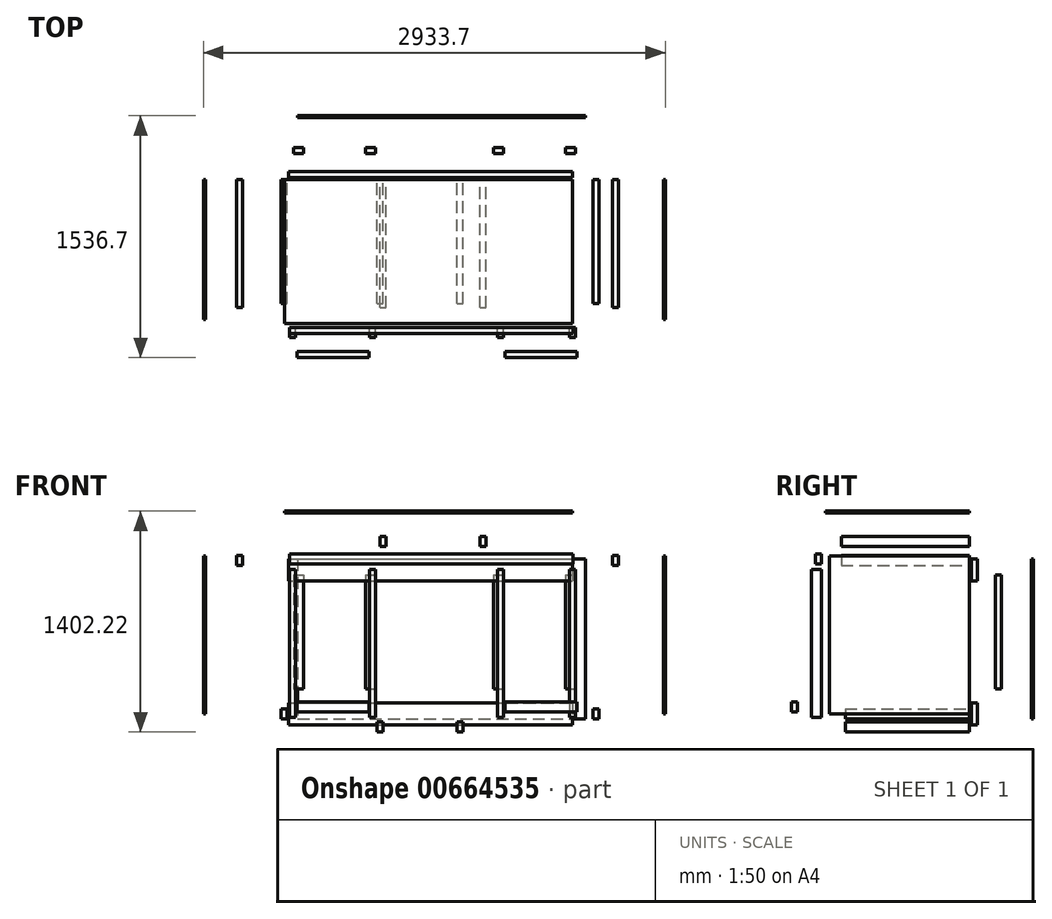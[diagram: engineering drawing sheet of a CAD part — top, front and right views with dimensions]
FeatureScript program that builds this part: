
annotation { "Feature Type Name" : "Feature", "Feature Type Description" : "" }
export const myFeature = defineFeature(function(context is Context, id is Id, definition is map)
    precondition{}
    {
        {
            var Q0;
            Q0=qCreatedBy(makeId("Front.planeOp"),FACE);
            var sketch = newSketch(context, id + "F0", { "sketchPlane" : qUnion([Q0])});
            skLineSegment(sketch, "E0.bottom", {"start": v(-77.6, 167.5) * mm, "end": v(1751.2, 167.5) * mm});
            skLineSegment(sketch, "E0.top", {"start": v(-77.6, 154.8) * mm, "end": v(1751.2, 154.8) * mm});
            skLineSegment(sketch, "E0.left", {"start": v(-77.6, 167.5) * mm, "end": v(-77.6, 154.8) * mm});
            skLineSegment(sketch, "E0.right", {"start": v(1751.2, 167.5) * mm, "end": v(1751.2, 154.8) * mm});
            skSolve(sketch);
        }
        {
            var Q0;
            Q0 = qSketchRegion(id + "F0", true);
            extrude(context, id + "F1", {"entities" : qUnion([Q0]), "depth" : 914.4 * mm, "offsetDistance" : 25.4 * mm});
        }
        {
            var Q0;
            Q0=qCreatedBy(makeId("Front.planeOp"),FACE);
            var sketch = newSketch(context, id + "F2", { "sketchPlane" : qUnion([Q0])});
            skLineSegment(sketch, "E1.bottom", {"start": v(-96.67, 148.12) * mm, "end": v(1706.73, 148.12) * mm});
            skLineSegment(sketch, "E1.top", {"start": v(-96.67, 84.62) * mm, "end": v(1706.73, 84.62) * mm});
            skLineSegment(sketch, "E1.left", {"start": v(-96.67, 148.12) * mm, "end": v(-96.67, 84.62) * mm});
            skLineSegment(sketch, "E1.right", {"start": v(1706.73, 148.12) * mm, "end": v(1706.73, 84.62) * mm});
            skSolve(sketch);
        }
        {
            var Q0;
            Q0 = qSketchRegion(id + "F2", true);
            extrude(context, id + "F3", {"entities" : qUnion([Q0]), "depth" : 38.1 * mm, "offsetDistance" : 25.4 * mm});
        }
        {
            var Q0;
            Q0=makeQuery(id+"F3.opExtrude","SWEPT_BODY",BODY,{"disambiguationData":[OSD([sQuery(id+"F2.wireOp",EDGE,"E1.bottom"),sQuery(id+"F2.wireOp",EDGE,"E1.top"),sQuery(id+"F2.wireOp",EDGE,"E1.left"),sQuery(id+"F2.wireOp",EDGE,"E1.right")])]});
            transform(context, id + "F4", {"entities" : qUnion([Q0]), "transformType" : TransformType.TRANSLATION_3D, "dx" : -762 * mm, "dy" : -939.8 * mm, "dz" : 0 * mm, "makeCopy" : false});
        }
        {
            var Q0;
            Q0=makeQuery(id+"F1.opExtrude","SWEPT_BODY",BODY,{"disambiguationData":[OSD([sQuery(id+"F0.wireOp",EDGE,"E0.bottom"),sQuery(id+"F0.wireOp",EDGE,"E0.top"),sQuery(id+"F0.wireOp",EDGE,"E0.left"),sQuery(id+"F0.wireOp",EDGE,"E0.right")])]});
            transform(context, id + "F5", {"entities" : qUnion([Q0]), "transformType" : TransformType.TRANSLATION_3D, "dx" : -812.8 * mm, "dy" : 0 * mm, "dz" : 0 * mm, "makeCopy" : false});
        }
        {
            var Q0;
            Q0=qCreatedBy(makeId("Front.planeOp"),FACE);
            var sketch = newSketch(context, id + "F6", { "sketchPlane" : qUnion([Q0])});
            skLineSegment(sketch, "E2.bottom", {"start": v(-857.8, 557.43) * mm, "end": v(-819.7, 557.43) * mm});
            skLineSegment(sketch, "E2.top", {"start": v(-857.8, -382.37) * mm, "end": v(-819.7, -382.37) * mm});
            skLineSegment(sketch, "E2.left", {"start": v(-857.8, 557.43) * mm, "end": v(-857.8, -382.37) * mm});
            skLineSegment(sketch, "E2.right", {"start": v(-819.7, 557.43) * mm, "end": v(-819.7, -382.37) * mm});
            skSolve(sketch);
        }
        {
            var Q0;
            Q0 = qSketchRegion(id + "F6", true);
            extrude(context, id + "F7", {"entities" : qUnion([Q0]), "depth" : 63.5 * mm, "offsetDistance" : 25.4 * mm});
        }
        {
            var Q0;
            Q0=makeQuery(id+"F7.opExtrude","SWEPT_BODY",BODY,{"disambiguationData":[OSD([sQuery(id+"F6.wireOp",EDGE,"E2.bottom"),sQuery(id+"F6.wireOp",EDGE,"E2.top"),sQuery(id+"F6.wireOp",EDGE,"E2.left"),sQuery(id+"F6.wireOp",EDGE,"E2.right")])]});
            transform(context, id + "F8", {"entities" : qUnion([Q0]), "transformType" : TransformType.TRANSLATION_3D, "dx" : 0 * mm, "dy" : -939.8 * mm, "dz" : -508 * mm, "makeCopy" : false});
        }
        {
            var Q0;
            Q0=makeQuery(id+"F7.opExtrude","SWEPT_BODY",BODY,{"disambiguationData":[OSD([sQuery(id+"F6.wireOp",EDGE,"E2.bottom"),sQuery(id+"F6.wireOp",EDGE,"E2.top"),sQuery(id+"F6.wireOp",EDGE,"E2.left"),sQuery(id+"F6.wireOp",EDGE,"E2.right")])]});
            transform(context, id + "F9", {"entities" : qUnion([Q0]), "transformType" : TransformType.TRANSLATION_3D, "dx" : 1778 * mm, "dy" : 0 * mm, "dz" : 0 * mm, "makeCopy" : true});
        }
        {
            var Q0;
            Q0=makeQuery(id+"F7.opExtrude","SWEPT_BODY",BODY,{"disambiguationData":[OSD([sQuery(id+"F6.wireOp",EDGE,"E2.bottom"),sQuery(id+"F6.wireOp",EDGE,"E2.top"),sQuery(id+"F6.wireOp",EDGE,"E2.left"),sQuery(id+"F6.wireOp",EDGE,"E2.right")])]});
            transform(context, id + "F10", {"entities" : qUnion([Q0]), "transformType" : TransformType.TRANSLATION_3D, "dx" : 508 * mm, "dy" : 0 * mm, "dz" : 0 * mm, "makeCopy" : true});
        }
        {
            var Q0;
            Q0=makeQuery(id+"F7.opExtrude","SWEPT_BODY",BODY,{"disambiguationData":[OSD([sQuery(id+"F6.wireOp",EDGE,"E2.bottom"),sQuery(id+"F6.wireOp",EDGE,"E2.top"),sQuery(id+"F6.wireOp",EDGE,"E2.left"),sQuery(id+"F6.wireOp",EDGE,"E2.right")])]});
            transform(context, id + "F11", {"entities" : qUnion([Q0]), "transformType" : TransformType.TRANSLATION_3D, "dx" : 1320.8 * mm, "dy" : 0 * mm, "dz" : 0 * mm, "makeCopy" : true});
        }
        {
            var Q0;
            Q0=qCreatedBy(makeId("Front.planeOp"),FACE);
            var sketch = newSketch(context, id + "F12", { "sketchPlane" : qUnion([Q0])});
            skLineSegment(sketch, "E3.bottom", {"start": v(-940.02, 138.97) * mm, "end": v(-901.92, 138.97) * mm});
            skLineSegment(sketch, "E3.top", {"start": v(-940.02, 75.47) * mm, "end": v(-901.92, 75.47) * mm});
            skLineSegment(sketch, "E3.left", {"start": v(-940.02, 138.97) * mm, "end": v(-940.02, 75.47) * mm});
            skLineSegment(sketch, "E3.right", {"start": v(-901.92, 138.97) * mm, "end": v(-901.92, 75.47) * mm});
            skSolve(sketch);
        }
        {
            var Q0;
            Q0 = qSketchRegion(id + "F12", true);
            extrude(context, id + "F13", {"entities" : qUnion([Q0]), "depth" : 812.8 * mm, "offsetDistance" : 25.4 * mm});
        }
        {
            var Q0;
            Q0=makeQuery(id+"F13.opExtrude","SWEPT_BODY",BODY,{"disambiguationData":[OSD([sQuery(id+"F12.wireOp",EDGE,"E3.bottom"),sQuery(id+"F12.wireOp",EDGE,"E3.top"),sQuery(id+"F12.wireOp",EDGE,"E3.left"),sQuery(id+"F12.wireOp",EDGE,"E3.right")])]});
            transform(context, id + "F14", {"entities" : qUnion([Q0]), "transformType" : TransformType.TRANSLATION_3D, "dx" : 1879.6 * mm, "dy" : 0 * mm, "dz" : 0 * mm, "makeCopy" : true});
        }
        {
            var Q0;
            Q0=qCreatedBy(makeId("Front.planeOp"),FACE);
            var sketch = newSketch(context, id + "F15", { "sketchPlane" : qUnion([Q0])});
            skLineSegment(sketch, "E4.bottom", {"start": v(-862.45, 42) * mm, "end": v(940.95, 42) * mm});
            skLineSegment(sketch, "E4.top", {"start": v(-862.45, -97.7) * mm, "end": v(940.95, -97.7) * mm});
            skLineSegment(sketch, "E4.left", {"start": v(-862.45, 42) * mm, "end": v(-862.45, -97.7) * mm});
            skLineSegment(sketch, "E4.right", {"start": v(940.95, 42) * mm, "end": v(940.95, -97.7) * mm});
            skSolve(sketch);
        }
        {
            var Q0;
            Q0 = qSketchRegion(id + "F15", true);
            extrude(context, id + "F16", {"entities" : qUnion([Q0]), "depth" : 38.1 * mm, "offsetDistance" : 25.4 * mm});
        }
        {
            var Q0;
            Q0=makeQuery(id+"F16.opExtrude","SWEPT_BODY",BODY,{"disambiguationData":[OSD([sQuery(id+"F15.wireOp",EDGE,"E4.bottom"),sQuery(id+"F15.wireOp",EDGE,"E4.top"),sQuery(id+"F15.wireOp",EDGE,"E4.left"),sQuery(id+"F15.wireOp",EDGE,"E4.right")])]});
            transform(context, id + "F17", {"entities" : qUnion([Q0]), "transformType" : TransformType.TRANSLATION_3D, "dx" : 0 * mm, "dy" : 0 * mm, "dz" : -762 * mm, "makeCopy" : true});
        }
        {
            var Q0;
            Q0=makeQuery(id+"F13.opExtrude","SWEPT_BODY",BODY,{"disambiguationData":[OSD([sQuery(id+"F12.wireOp",EDGE,"E3.bottom"),sQuery(id+"F12.wireOp",EDGE,"E3.top"),sQuery(id+"F12.wireOp",EDGE,"E3.left"),sQuery(id+"F12.wireOp",EDGE,"E3.right")])]});
            transform(context, id + "F18", {"entities" : qUnion([Q0]), "transformType" : TransformType.TRANSLATION_3D, "dx" : 0 * mm, "dy" : 0 * mm, "dz" : -939.8 * mm, "makeCopy" : true});
        }
        {
            var Q0;
            Q0=makeQuery(id+"F14.opPattern","COPY",BODY,{"derivedFrom":makeQuery(id+"F13.opExtrude","SWEPT_BODY",BODY,{"disambiguationData":[OSD([sQuery(id+"F12.wireOp",EDGE,"E3.bottom"),sQuery(id+"F12.wireOp",EDGE,"E3.top"),sQuery(id+"F12.wireOp",EDGE,"E3.left"),sQuery(id+"F12.wireOp",EDGE,"E3.right")])]}),"instanceName":"1"});
            transform(context, id + "F19", {"entities" : qUnion([Q0]), "transformType" : TransformType.TRANSLATION_3D, "dx" : 0 * mm, "dy" : 0 * mm, "dz" : -939.8 * mm, "makeCopy" : true});
        }
        {
            var Q0;
            Q0=qCreatedBy(makeId("Front.planeOp"),FACE);
            var sketch = newSketch(context, id + "F20", { "sketchPlane" : qUnion([Q0])});
            skLineSegment(sketch, "E5.bottom", {"start": v(-809.8, -791.75) * mm, "end": v(-352.6, -791.75) * mm});
            skLineSegment(sketch, "E5.top", {"start": v(-809.8, -855.25) * mm, "end": v(-352.6, -855.25) * mm});
            skLineSegment(sketch, "E5.left", {"start": v(-809.8, -791.75) * mm, "end": v(-809.8, -855.25) * mm});
            skLineSegment(sketch, "E5.right", {"start": v(-352.6, -791.75) * mm, "end": v(-352.6, -855.25) * mm});
            skSolve(sketch);
        }
        {
            var Q0;
            Q0 = qSketchRegion(id + "F20", true);
            extrude(context, id + "F21", {"entities" : qUnion([Q0]), "depth" : 38.1 * mm, "offsetDistance" : 25.4 * mm});
        }
        {
            var Q0;
            Q0=makeQuery(id+"F21.opExtrude","SWEPT_BODY",BODY,{"disambiguationData":[OSD([sQuery(id+"F20.wireOp",EDGE,"E5.bottom"),sQuery(id+"F20.wireOp",EDGE,"E5.top"),sQuery(id+"F20.wireOp",EDGE,"E5.left"),sQuery(id+"F20.wireOp",EDGE,"E5.right")])]});
            transform(context, id + "F22", {"entities" : qUnion([Q0]), "transformType" : TransformType.TRANSLATION_3D, "dx" : 0 * mm, "dy" : -965.2 * mm, "dz" : 0 * mm, "makeCopy" : false});
        }
        {
            var Q0;
            Q0=makeQuery(id+"F21.opExtrude","SWEPT_BODY",BODY,{"disambiguationData":[OSD([sQuery(id+"F20.wireOp",EDGE,"E5.bottom"),sQuery(id+"F20.wireOp",EDGE,"E5.top"),sQuery(id+"F20.wireOp",EDGE,"E5.left"),sQuery(id+"F20.wireOp",EDGE,"E5.right")])]});
            transform(context, id + "F23", {"entities" : qUnion([Q0]), "transformType" : TransformType.TRANSLATION_3D, "dx" : 1320.8 * mm, "dy" : 0 * mm, "dz" : 0 * mm, "makeCopy" : true});
        }
        {
            var Q0;
            Q0=makeQuery(id+"F13.opExtrude","SWEPT_BODY",BODY,{"disambiguationData":[OSD([sQuery(id+"F12.wireOp",EDGE,"E3.bottom"),sQuery(id+"F12.wireOp",EDGE,"E3.top"),sQuery(id+"F12.wireOp",EDGE,"E3.left"),sQuery(id+"F12.wireOp",EDGE,"E3.right")])]});
            transform(context, id + "F24", {"entities" : qUnion([Q0]), "transformType" : TransformType.TRANSLATION_3D, "dx" : 508 * mm, "dy" : 0 * mm, "dz" : 0 * mm, "makeCopy" : true});
        }
        {
            var Q0;
            Q0=makeQuery(id+"F13.opExtrude","SWEPT_BODY",BODY,{"disambiguationData":[OSD([sQuery(id+"F12.wireOp",EDGE,"E3.bottom"),sQuery(id+"F12.wireOp",EDGE,"E3.top"),sQuery(id+"F12.wireOp",EDGE,"E3.left"),sQuery(id+"F12.wireOp",EDGE,"E3.right")])]});
            transform(context, id + "F25", {"entities" : qUnion([Q0]), "transformType" : TransformType.TRANSLATION_3D, "dx" : 1320.8 * mm, "dy" : 0 * mm, "dz" : 0 * mm, "makeCopy" : true});
        }
        {
            var Q0;
            Q0=qCreatedBy(makeId("Front.planeOp"),FACE);
            var sketch = newSketch(context, id + "F26", { "sketchPlane" : qUnion([Q0])});
            skLineSegment(sketch, "E6.bottom", {"start": v(-831.16, 15.51) * mm, "end": v(-767.66, 15.51) * mm});
            skLineSegment(sketch, "E6.top", {"start": v(-831.16, -708.39) * mm, "end": v(-767.66, -708.39) * mm});
            skLineSegment(sketch, "E6.left", {"start": v(-831.16, 15.51) * mm, "end": v(-831.16, -708.39) * mm});
            skLineSegment(sketch, "E6.right", {"start": v(-767.66, 15.51) * mm, "end": v(-767.66, -708.39) * mm});
            skSolve(sketch);
        }
        {
            var Q0;
            Q0 = qSketchRegion(id + "F26", true);
            extrude(context, id + "F27", {"entities" : qUnion([Q0]), "depth" : 38.1 * mm, "offsetDistance" : 25.4 * mm});
        }
        {
            var Q0;
            Q0=makeQuery(id+"F27.opExtrude","SWEPT_BODY",BODY,{"disambiguationData":[OSD([sQuery(id+"F26.wireOp",EDGE,"E6.bottom"),sQuery(id+"F26.wireOp",EDGE,"E6.top"),sQuery(id+"F26.wireOp",EDGE,"E6.left"),sQuery(id+"F26.wireOp",EDGE,"E6.right")])]});
            transform(context, id + "F28", {"entities" : qUnion([Q0]), "transformType" : TransformType.TRANSLATION_3D, "dx" : 0 * mm, "dy" : 76.2 * mm, "dz" : 0 * mm, "makeCopy" : false});
        }
        {
            var Q0;
            Q0=makeQuery(id+"F27.opExtrude","SWEPT_BODY",BODY,{"disambiguationData":[OSD([sQuery(id+"F26.wireOp",EDGE,"E6.bottom"),sQuery(id+"F26.wireOp",EDGE,"E6.top"),sQuery(id+"F26.wireOp",EDGE,"E6.left"),sQuery(id+"F26.wireOp",EDGE,"E6.right")])]});
            transform(context, id + "F29", {"entities" : qUnion([Q0]), "transformType" : TransformType.TRANSLATION_3D, "dx" : 457.2 * mm, "dy" : 0 * mm, "dz" : 0 * mm, "makeCopy" : true});
        }
        {
            var Q0;
            Q0=makeQuery(id+"F27.opExtrude","SWEPT_BODY",BODY,{"disambiguationData":[OSD([sQuery(id+"F26.wireOp",EDGE,"E6.bottom"),sQuery(id+"F26.wireOp",EDGE,"E6.top"),sQuery(id+"F26.wireOp",EDGE,"E6.left"),sQuery(id+"F26.wireOp",EDGE,"E6.right")])]});
            transform(context, id + "F30", {"entities" : qUnion([Q0]), "transformType" : TransformType.TRANSLATION_3D, "dx" : 1270 * mm, "dy" : 0 * mm, "dz" : 0 * mm, "makeCopy" : true});
        }
        {
            var Q0;
            Q0=makeQuery(id+"F27.opExtrude","SWEPT_BODY",BODY,{"disambiguationData":[OSD([sQuery(id+"F26.wireOp",EDGE,"E6.bottom"),sQuery(id+"F26.wireOp",EDGE,"E6.top"),sQuery(id+"F26.wireOp",EDGE,"E6.left"),sQuery(id+"F26.wireOp",EDGE,"E6.right")])]});
            transform(context, id + "F31", {"entities" : qUnion([Q0]), "transformType" : TransformType.TRANSLATION_3D, "dx" : 1727.2 * mm, "dy" : 0 * mm, "dz" : 0 * mm, "makeCopy" : true});
        }
        {
            var Q0;
            Q0=qCreatedBy(makeId("Front.planeOp"),FACE);
            var sketch = newSketch(context, id + "F32", { "sketchPlane" : qUnion([Q0])});
            skLineSegment(sketch, "E7.bottom", {"start": v(-1023.09, 135.28) * mm, "end": v(-1010.39, 135.28) * mm});
            skLineSegment(sketch, "E7.top", {"start": v(-1023.09, -868.02) * mm, "end": v(-1010.39, -868.02) * mm});
            skLineSegment(sketch, "E7.left", {"start": v(-1023.09, 135.28) * mm, "end": v(-1023.09, -868.02) * mm});
            skLineSegment(sketch, "E7.right", {"start": v(-1010.39, 135.28) * mm, "end": v(-1010.39, -868.02) * mm});
            skSolve(sketch);
        }
        {
            var Q0;
            Q0 = qSketchRegion(id + "F32", true);
            extrude(context, id + "F33", {"entities" : qUnion([Q0]), "depth" : 889 * mm, "offsetDistance" : 25.4 * mm});
        }
        {
            var Q0;
            Q0=makeQuery(id+"F33.opExtrude","SWEPT_BODY",BODY,{"disambiguationData":[OSD([sQuery(id+"F32.wireOp",EDGE,"E7.bottom"),sQuery(id+"F32.wireOp",EDGE,"E7.top"),sQuery(id+"F32.wireOp",EDGE,"E7.left"),sQuery(id+"F32.wireOp",EDGE,"E7.right")])]});
            transform(context, id + "F34", {"entities" : qUnion([Q0]), "transformType" : TransformType.TRANSLATION_3D, "dx" : 2032 * mm, "dy" : 0 * mm, "dz" : 0 * mm, "makeCopy" : true});
        }
        {
            var Q0;
            Q0=qCreatedBy(makeId("Front.planeOp"),FACE);
            var sketch = newSketch(context, id + "F35", { "sketchPlane" : qUnion([Q0])});
            skLineSegment(sketch, "E8.bottom", {"start": v(-806.57, 117.24) * mm, "end": v(1022.23, 117.24) * mm});
            skLineSegment(sketch, "E8.top", {"start": v(-806.57, -898.76) * mm, "end": v(1022.23, -898.76) * mm});
            skLineSegment(sketch, "E8.left", {"start": v(-806.57, 117.24) * mm, "end": v(-806.57, -898.76) * mm});
            skLineSegment(sketch, "E8.right", {"start": v(1022.23, 117.24) * mm, "end": v(1022.23, -898.76) * mm});
            skSolve(sketch);
        }
        {
            var Q0;
            Q0 = qSketchRegion(id + "F35", true);
            extrude(context, id + "F36", {"entities" : qUnion([Q0]), "depth" : 12.7 * mm, "offsetDistance" : 25.4 * mm});
        }
        {
            var Q0;
            Q0=makeQuery(id+"F36.opExtrude","SWEPT_BODY",BODY,{"disambiguationData":[OSD([sQuery(id+"F35.wireOp",EDGE,"E8.bottom"),sQuery(id+"F35.wireOp",EDGE,"E8.top"),sQuery(id+"F35.wireOp",EDGE,"E8.left"),sQuery(id+"F35.wireOp",EDGE,"E8.right")])]});
            transform(context, id + "F37", {"entities" : qUnion([Q0]), "transformType" : TransformType.TRANSLATION_3D, "dx" : 0 * mm, "dy" : 152.4 * mm, "dz" : 0 * mm, "makeCopy" : false});
        }
        {
            var Q0;
            Q0=qCreatedBy(makeId("Front.planeOp"),FACE);
            var sketch = newSketch(context, id + "F38", { "sketchPlane" : qUnion([Q0])});
            skLineSegment(sketch, "E9.bottom", {"start": v(-300.73, -790.22) * mm, "end": v(-262.63, -790.22) * mm});
            skLineSegment(sketch, "E9.top", {"start": v(-300.73, -853.72) * mm, "end": v(-262.63, -853.72) * mm});
            skLineSegment(sketch, "E9.left", {"start": v(-300.73, -790.22) * mm, "end": v(-300.73, -853.72) * mm});
            skLineSegment(sketch, "E9.right", {"start": v(-262.63, -790.22) * mm, "end": v(-262.63, -853.72) * mm});
            skSolve(sketch);
        }
        {
            var Q0;
            Q0 = qSketchRegion(id + "F38", true);
            extrude(context, id + "F39", {"entities" : qUnion([Q0]), "depth" : 787.4 * mm, "offsetDistance" : 25.4 * mm});
        }
        {
            var Q0;
            Q0=makeQuery(id+"F39.opExtrude","SWEPT_BODY",BODY,{"disambiguationData":[OSD([sQuery(id+"F38.wireOp",EDGE,"E9.bottom"),sQuery(id+"F38.wireOp",EDGE,"E9.top"),sQuery(id+"F38.wireOp",EDGE,"E9.left"),sQuery(id+"F38.wireOp",EDGE,"E9.right")])]});
            transform(context, id + "F40", {"entities" : qUnion([Q0]), "transformType" : TransformType.TRANSLATION_3D, "dx" : 508 * mm, "dy" : 0 * mm, "dz" : 0 * mm, "makeCopy" : true});
        }
        {
            var Q0;
            Q0=makeQuery(id+"F19.opPattern","COPY",BODY,{"derivedFrom":makeQuery(id+"F14.opPattern","COPY",BODY,{"derivedFrom":makeQuery(id+"F13.opExtrude","SWEPT_BODY",BODY,{"disambiguationData":[OSD([sQuery(id+"F12.wireOp",EDGE,"E3.bottom"),sQuery(id+"F12.wireOp",EDGE,"E3.top"),sQuery(id+"F12.wireOp",EDGE,"E3.left"),sQuery(id+"F12.wireOp",EDGE,"E3.right")])]}),"instanceName":"1"}),"instanceName":"1"});
            deleteBodies(context, id + "F41", {"entities" : qUnion([Q0])});
        }
        {
            var Q0;
            Q0=makeQuery(id+"F18.opPattern","COPY",BODY,{"derivedFrom":makeQuery(id+"F13.opExtrude","SWEPT_BODY",BODY,{"disambiguationData":[OSD([sQuery(id+"F12.wireOp",EDGE,"E3.bottom"),sQuery(id+"F12.wireOp",EDGE,"E3.top"),sQuery(id+"F12.wireOp",EDGE,"E3.left"),sQuery(id+"F12.wireOp",EDGE,"E3.right")])]}),"instanceName":"1"});
            deleteBodies(context, id + "F42", {"entities" : qUnion([Q0])});
        }
        {
            var Q0;
            Q0=makeQuery(id+"F24.opPattern","COPY",BODY,{"derivedFrom":makeQuery(id+"F13.opExtrude","SWEPT_BODY",BODY,{"disambiguationData":[OSD([sQuery(id+"F12.wireOp",EDGE,"E3.bottom"),sQuery(id+"F12.wireOp",EDGE,"E3.top"),sQuery(id+"F12.wireOp",EDGE,"E3.left"),sQuery(id+"F12.wireOp",EDGE,"E3.right")])]}),"instanceName":"1"});
            deleteBodies(context, id + "F43", {"entities" : qUnion([Q0])});
        }
        {
            var Q0;
            Q0=makeQuery(id+"F25.opPattern","COPY",BODY,{"derivedFrom":makeQuery(id+"F13.opExtrude","SWEPT_BODY",BODY,{"disambiguationData":[OSD([sQuery(id+"F12.wireOp",EDGE,"E3.bottom"),sQuery(id+"F12.wireOp",EDGE,"E3.top"),sQuery(id+"F12.wireOp",EDGE,"E3.left"),sQuery(id+"F12.wireOp",EDGE,"E3.right")])]}),"instanceName":"1"});
            deleteBodies(context, id + "F44", {"entities" : qUnion([Q0])});
        }
        {
            var Q0;
            Q0=qCreatedBy(makeId("Front.planeOp"),FACE);
            var sketch = newSketch(context, id + "F45", { "sketchPlane" : qUnion([Q0])});
            skLineSegment(sketch, "E10.bottom", {"start": v(-911.41, -835.62) * mm, "end": v(-873.31, -835.62) * mm});
            skLineSegment(sketch, "E10.top", {"start": v(-911.41, -899.12) * mm, "end": v(-873.31, -899.12) * mm});
            skLineSegment(sketch, "E10.left", {"start": v(-911.41, -835.62) * mm, "end": v(-911.41, -899.12) * mm});
            skLineSegment(sketch, "E10.right", {"start": v(-873.31, -835.62) * mm, "end": v(-873.31, -899.12) * mm});
            skSolve(sketch);
        }
        {
            var Q0;
            Q0 = qSketchRegion(id + "F45", true);
            extrude(context, id + "F46", {"entities" : qUnion([Q0]), "depth" : 787.4 * mm, "offsetDistance" : 25.4 * mm});
        }
        {
            var Q0;
            Q0=makeQuery(id+"F46.opExtrude","SWEPT_BODY",BODY,{"disambiguationData":[OSD([sQuery(id+"F45.wireOp",EDGE,"E10.bottom"),sQuery(id+"F45.wireOp",EDGE,"E10.top"),sQuery(id+"F45.wireOp",EDGE,"E10.left"),sQuery(id+"F45.wireOp",EDGE,"E10.right")])]});
            transform(context, id + "F47", {"entities" : qUnion([Q0]), "transformType" : TransformType.TRANSLATION_3D, "dx" : 1981.2 * mm, "dy" : 0 * mm, "dz" : 0 * mm, "makeCopy" : true});
        }
        {
            var Q0;
            Q0=makeQuery(id+"F46.opExtrude","SWEPT_BODY",BODY,{"disambiguationData":[OSD([sQuery(id+"F45.wireOp",EDGE,"E10.bottom"),sQuery(id+"F45.wireOp",EDGE,"E10.top"),sQuery(id+"F45.wireOp",EDGE,"E10.left"),sQuery(id+"F45.wireOp",EDGE,"E10.right")])]});
            transform(context, id + "F48", {"entities" : qUnion([Q0]), "transformType" : TransformType.TRANSLATION_3D, "dx" : 533.4 * mm, "dy" : 0 * mm, "dz" : 762 * mm, "makeCopy" : true});
        }
        {
            var Q0;
            Q0=makeQuery(id+"F48.opPattern","COPY",BODY,{"derivedFrom":makeQuery(id+"F46.opExtrude","SWEPT_BODY",BODY,{"disambiguationData":[OSD([sQuery(id+"F45.wireOp",EDGE,"E10.bottom"),sQuery(id+"F45.wireOp",EDGE,"E10.top"),sQuery(id+"F45.wireOp",EDGE,"E10.left"),sQuery(id+"F45.wireOp",EDGE,"E10.right")])]}),"instanceName":"1"});
            transform(context, id + "F49", {"entities" : qUnion([Q0]), "transformType" : TransformType.TRANSLATION_3D, "dx" : 635 * mm, "dy" : 0 * mm, "dz" : 0 * mm, "makeCopy" : true});
        }
        {
            var Q0;
            Q0=makeQuery(id+"F48.opPattern","COPY",BODY,{"derivedFrom":makeQuery(id+"F46.opExtrude","SWEPT_BODY",BODY,{"disambiguationData":[OSD([sQuery(id+"F45.wireOp",EDGE,"E10.bottom"),sQuery(id+"F45.wireOp",EDGE,"E10.top"),sQuery(id+"F45.wireOp",EDGE,"E10.left"),sQuery(id+"F45.wireOp",EDGE,"E10.right")])]}),"instanceName":"1"});
            deleteBodies(context, id + "F50", {"entities" : qUnion([Q0])});
        }
        {
            var Q0;
            Q0=makeQuery(id+"F49.opPattern","COPY",BODY,{"derivedFrom":makeQuery(id+"F48.opPattern","COPY",BODY,{"derivedFrom":makeQuery(id+"F46.opExtrude","SWEPT_BODY",BODY,{"disambiguationData":[OSD([sQuery(id+"F45.wireOp",EDGE,"E10.bottom"),sQuery(id+"F45.wireOp",EDGE,"E10.top"),sQuery(id+"F45.wireOp",EDGE,"E10.left"),sQuery(id+"F45.wireOp",EDGE,"E10.right")])]}),"instanceName":"1"}),"instanceName":"1"});
            deleteBodies(context, id + "F51", {"entities" : qUnion([Q0])});
        }
        {
            var Q0;
            Q0=qCreatedBy(makeId("Front.planeOp"),FACE);
            var sketch = newSketch(context, id + "F52", { "sketchPlane" : qUnion([Q0])});
            skLineSegment(sketch, "E11.bottom", {"start": v(-283.08, 7.53) * mm, "end": v(-244.98, 7.53) * mm});
            skLineSegment(sketch, "E11.top", {"start": v(-283.08, -55.97) * mm, "end": v(-244.98, -55.97) * mm});
            skLineSegment(sketch, "E11.left", {"start": v(-283.08, 7.53) * mm, "end": v(-283.08, -55.97) * mm});
            skLineSegment(sketch, "E11.right", {"start": v(-244.98, 7.53) * mm, "end": v(-244.98, -55.97) * mm});
            skSolve(sketch);
        }
        {
            var Q0;
            Q0 = qSketchRegion(id + "F52", true);
            extrude(context, id + "F53", {"entities" : qUnion([Q0]), "depth" : 812.8 * mm, "offsetDistance" : 25.4 * mm});
        }
        {
            var Q0;
            Q0=makeQuery(id+"F53.opExtrude","SWEPT_BODY",BODY,{"disambiguationData":[OSD([sQuery(id+"F52.wireOp",EDGE,"E11.bottom"),sQuery(id+"F52.wireOp",EDGE,"E11.top"),sQuery(id+"F52.wireOp",EDGE,"E11.left"),sQuery(id+"F52.wireOp",EDGE,"E11.right")])]});
            transform(context, id + "F54", {"entities" : qUnion([Q0]), "transformType" : TransformType.TRANSLATION_3D, "dx" : 635 * mm, "dy" : 0 * mm, "dz" : 0 * mm, "makeCopy" : true});
        }
        {
            var Q0;
            Q0=makeQuery(id+"F33.opExtrude","SWEPT_BODY",BODY,{"disambiguationData":[OSD([sQuery(id+"F32.wireOp",EDGE,"E7.bottom"),sQuery(id+"F32.wireOp",EDGE,"E7.top"),sQuery(id+"F32.wireOp",EDGE,"E7.left"),sQuery(id+"F32.wireOp",EDGE,"E7.right")])]});
            transform(context, id + "F55", {"entities" : qUnion([Q0]), "transformType" : TransformType.TRANSLATION_3D, "dx" : -381 * mm, "dy" : 0 * mm, "dz" : 0 * mm, "makeCopy" : false});
        }
        {
            var Q0;
            Q0=makeQuery(id+"F34.opPattern","COPY",BODY,{"derivedFrom":makeQuery(id+"F33.opExtrude","SWEPT_BODY",BODY,{"disambiguationData":[OSD([sQuery(id+"F32.wireOp",EDGE,"E7.bottom"),sQuery(id+"F32.wireOp",EDGE,"E7.top"),sQuery(id+"F32.wireOp",EDGE,"E7.left"),sQuery(id+"F32.wireOp",EDGE,"E7.right")])]}),"instanceName":"1"});
            transform(context, id + "F56", {"entities" : qUnion([Q0]), "transformType" : TransformType.TRANSLATION_3D, "dx" : -2286 * mm, "dy" : 0 * mm, "dz" : 0 * mm, "makeCopy" : false});
        }
        {
            var Q0;
            Q0=makeQuery(id+"F34.opPattern","COPY",BODY,{"derivedFrom":makeQuery(id+"F33.opExtrude","SWEPT_BODY",BODY,{"disambiguationData":[OSD([sQuery(id+"F32.wireOp",EDGE,"E7.bottom"),sQuery(id+"F32.wireOp",EDGE,"E7.top"),sQuery(id+"F32.wireOp",EDGE,"E7.left"),sQuery(id+"F32.wireOp",EDGE,"E7.right")])]}),"instanceName":"1"});
            transform(context, id + "F57", {"entities" : qUnion([Q0]), "transformType" : TransformType.TRANSLATION_3D, "dx" : 2794 * mm, "dy" : 0 * mm, "dz" : 0 * mm, "makeCopy" : false});
        }
        {
            var Q0;
            Q0=makeQuery(id+"F1.opExtrude","SWEPT_BODY",BODY,{"disambiguationData":[OSD([sQuery(id+"F0.wireOp",EDGE,"E0.bottom"),sQuery(id+"F0.wireOp",EDGE,"E0.top"),sQuery(id+"F0.wireOp",EDGE,"E0.left"),sQuery(id+"F0.wireOp",EDGE,"E0.right")])]});
            transform(context, id + "F58", {"entities" : qUnion([Q0]), "transformType" : TransformType.TRANSLATION_3D, "dx" : 0 * mm, "dy" : 0 * mm, "dz" : 254 * mm, "makeCopy" : false});
        }
        {
            var Q0;
            Q0=makeQuery(id+"F36.opExtrude","SWEPT_BODY",BODY,{"disambiguationData":[OSD([sQuery(id+"F35.wireOp",EDGE,"E8.bottom"),sQuery(id+"F35.wireOp",EDGE,"E8.top"),sQuery(id+"F35.wireOp",EDGE,"E8.left"),sQuery(id+"F35.wireOp",EDGE,"E8.right")])]});
            transform(context, id + "F59", {"entities" : qUnion([Q0]), "transformType" : TransformType.TRANSLATION_3D, "dx" : 0 * mm, "dy" : 254 * mm, "dz" : 0 * mm, "makeCopy" : false});
        }
        {
            var Q0;
            Q0=makeQuery(id+"F13.opExtrude","SWEPT_BODY",BODY,{"disambiguationData":[OSD([sQuery(id+"F12.wireOp",EDGE,"E3.bottom"),sQuery(id+"F12.wireOp",EDGE,"E3.top"),sQuery(id+"F12.wireOp",EDGE,"E3.left"),sQuery(id+"F12.wireOp",EDGE,"E3.right")])]});
            transform(context, id + "F60", {"entities" : qUnion([Q0]), "transformType" : TransformType.TRANSLATION_3D, "dx" : -254 * mm, "dy" : 0 * mm, "dz" : 0 * mm, "makeCopy" : false});
        }
        {
            var Q0;
            Q0=makeQuery(id+"F14.opPattern","COPY",BODY,{"derivedFrom":makeQuery(id+"F13.opExtrude","SWEPT_BODY",BODY,{"disambiguationData":[OSD([sQuery(id+"F12.wireOp",EDGE,"E3.bottom"),sQuery(id+"F12.wireOp",EDGE,"E3.top"),sQuery(id+"F12.wireOp",EDGE,"E3.left"),sQuery(id+"F12.wireOp",EDGE,"E3.right")])]}),"instanceName":"1"});
            transform(context, id + "F61", {"entities" : qUnion([Q0]), "transformType" : TransformType.TRANSLATION_3D, "dx" : 254 * mm, "dy" : 0 * mm, "dz" : 0 * mm, "makeCopy" : false});
        }
        {
            var Q0;
            Q0=makeQuery(id+"F53.opExtrude","SWEPT_BODY",BODY,{"disambiguationData":[OSD([sQuery(id+"F52.wireOp",EDGE,"E11.bottom"),sQuery(id+"F52.wireOp",EDGE,"E11.top"),sQuery(id+"F52.wireOp",EDGE,"E11.left"),sQuery(id+"F52.wireOp",EDGE,"E11.right")])]});
            transform(context, id + "F62", {"entities" : qUnion([Q0]), "transformType" : TransformType.TRANSLATION_3D, "dx" : 0 * mm, "dy" : 0 * mm, "dz" : 254 * mm, "makeCopy" : false});
        }
        {
            var Q0;
            Q0=makeQuery(id+"F54.opPattern","COPY",BODY,{"derivedFrom":makeQuery(id+"F53.opExtrude","SWEPT_BODY",BODY,{"disambiguationData":[OSD([sQuery(id+"F52.wireOp",EDGE,"E11.bottom"),sQuery(id+"F52.wireOp",EDGE,"E11.top"),sQuery(id+"F52.wireOp",EDGE,"E11.left"),sQuery(id+"F52.wireOp",EDGE,"E11.right")])]}),"instanceName":"1"});
            transform(context, id + "F63", {"entities" : qUnion([Q0]), "transformType" : TransformType.TRANSLATION_3D, "dx" : 0 * mm, "dy" : 0 * mm, "dz" : 254 * mm, "makeCopy" : false});
        }
        {
            var Q0;
            Q0=makeQuery(id+"F27.opExtrude","SWEPT_BODY",BODY,{"disambiguationData":[OSD([sQuery(id+"F26.wireOp",EDGE,"E6.bottom"),sQuery(id+"F26.wireOp",EDGE,"E6.top"),sQuery(id+"F26.wireOp",EDGE,"E6.left"),sQuery(id+"F26.wireOp",EDGE,"E6.right")])]});
            var Q1;
            Q1=makeQuery(id+"F29.opPattern","COPY",BODY,{"derivedFrom":makeQuery(id+"F27.opExtrude","SWEPT_BODY",BODY,{"disambiguationData":[OSD([sQuery(id+"F26.wireOp",EDGE,"E6.bottom"),sQuery(id+"F26.wireOp",EDGE,"E6.top"),sQuery(id+"F26.wireOp",EDGE,"E6.left"),sQuery(id+"F26.wireOp",EDGE,"E6.right")])]}),"instanceName":"1"});
            var Q2;
            Q2=makeQuery(id+"F30.opPattern","COPY",BODY,{"derivedFrom":makeQuery(id+"F27.opExtrude","SWEPT_BODY",BODY,{"disambiguationData":[OSD([sQuery(id+"F26.wireOp",EDGE,"E6.bottom"),sQuery(id+"F26.wireOp",EDGE,"E6.top"),sQuery(id+"F26.wireOp",EDGE,"E6.left"),sQuery(id+"F26.wireOp",EDGE,"E6.right")])]}),"instanceName":"1"});
            var Q3;
            Q3=makeQuery(id+"F31.opPattern","COPY",BODY,{"derivedFrom":makeQuery(id+"F27.opExtrude","SWEPT_BODY",BODY,{"disambiguationData":[OSD([sQuery(id+"F26.wireOp",EDGE,"E6.bottom"),sQuery(id+"F26.wireOp",EDGE,"E6.top"),sQuery(id+"F26.wireOp",EDGE,"E6.left"),sQuery(id+"F26.wireOp",EDGE,"E6.right")])]}),"instanceName":"1"});
            transform(context, id + "F64", {"entities" : qUnion([Q0, Q1, Q2, Q3]), "transformType" : TransformType.TRANSLATION_3D, "dx" : 0 * mm, "dy" : 127 * mm, "dz" : 0 * mm, "makeCopy" : false});
        }
        {
            var Q0;
            Q0=makeQuery(id+"F21.opExtrude","SWEPT_BODY",BODY,{"disambiguationData":[OSD([sQuery(id+"F20.wireOp",EDGE,"E5.bottom"),sQuery(id+"F20.wireOp",EDGE,"E5.top"),sQuery(id+"F20.wireOp",EDGE,"E5.left"),sQuery(id+"F20.wireOp",EDGE,"E5.right")])]});
            var Q1;
            Q1=makeQuery(id+"F23.opPattern","COPY",BODY,{"derivedFrom":makeQuery(id+"F21.opExtrude","SWEPT_BODY",BODY,{"disambiguationData":[OSD([sQuery(id+"F20.wireOp",EDGE,"E5.bottom"),sQuery(id+"F20.wireOp",EDGE,"E5.top"),sQuery(id+"F20.wireOp",EDGE,"E5.left"),sQuery(id+"F20.wireOp",EDGE,"E5.right")])]}),"instanceName":"1"});
            transform(context, id + "F65", {"entities" : qUnion([Q0, Q1]), "transformType" : TransformType.TRANSLATION_3D, "dx" : 0 * mm, "dy" : -127 * mm, "dz" : 0 * mm, "makeCopy" : false});
        }
        {
            var Q0;
            Q0=makeQuery(id+"F39.opExtrude","SWEPT_BODY",BODY,{"disambiguationData":[OSD([sQuery(id+"F38.wireOp",EDGE,"E9.bottom"),sQuery(id+"F38.wireOp",EDGE,"E9.top"),sQuery(id+"F38.wireOp",EDGE,"E9.left"),sQuery(id+"F38.wireOp",EDGE,"E9.right")])]});
            transform(context, id + "F66", {"entities" : qUnion([Q0]), "transformType" : TransformType.TRANSLATION_3D, "dx" : 0 * mm, "dy" : 0 * mm, "dz" : -127 * mm, "makeCopy" : false});
        }
        {
            var Q0;
            Q0=makeQuery(id+"F40.opPattern","COPY",BODY,{"derivedFrom":makeQuery(id+"F39.opExtrude","SWEPT_BODY",BODY,{"disambiguationData":[OSD([sQuery(id+"F38.wireOp",EDGE,"E9.bottom"),sQuery(id+"F38.wireOp",EDGE,"E9.top"),sQuery(id+"F38.wireOp",EDGE,"E9.left"),sQuery(id+"F38.wireOp",EDGE,"E9.right")])]}),"instanceName":"1"});
            transform(context, id + "F67", {"entities" : qUnion([Q0]), "transformType" : TransformType.TRANSLATION_3D, "dx" : 0 * mm, "dy" : 0 * mm, "dz" : -127 * mm, "makeCopy" : false});
        }
        {
            var Q0;
            Q0=makeQuery(id+"F16.opExtrude","SWEPT_BODY",BODY,{"disambiguationData":[OSD([sQuery(id+"F15.wireOp",EDGE,"E4.bottom"),sQuery(id+"F15.wireOp",EDGE,"E4.top"),sQuery(id+"F15.wireOp",EDGE,"E4.left"),sQuery(id+"F15.wireOp",EDGE,"E4.right")])]});
            transform(context, id + "F68", {"entities" : qUnion([Q0]), "transformType" : TransformType.TRANSLATION_3D, "dx" : 0 * mm, "dy" : 50.8 * mm, "dz" : 76.2 * mm, "makeCopy" : false});
        }
        {
            var Q0;
            Q0=makeQuery(id+"F17.opPattern","COPY",BODY,{"derivedFrom":makeQuery(id+"F16.opExtrude","SWEPT_BODY",BODY,{"disambiguationData":[OSD([sQuery(id+"F15.wireOp",EDGE,"E4.bottom"),sQuery(id+"F15.wireOp",EDGE,"E4.top"),sQuery(id+"F15.wireOp",EDGE,"E4.left"),sQuery(id+"F15.wireOp",EDGE,"E4.right")])]}),"instanceName":"1"});
            transform(context, id + "F69", {"entities" : qUnion([Q0]), "transformType" : TransformType.TRANSLATION_3D, "dx" : 0 * mm, "dy" : 50.8 * mm, "dz" : -76.2 * mm, "makeCopy" : false});
        }
    });
